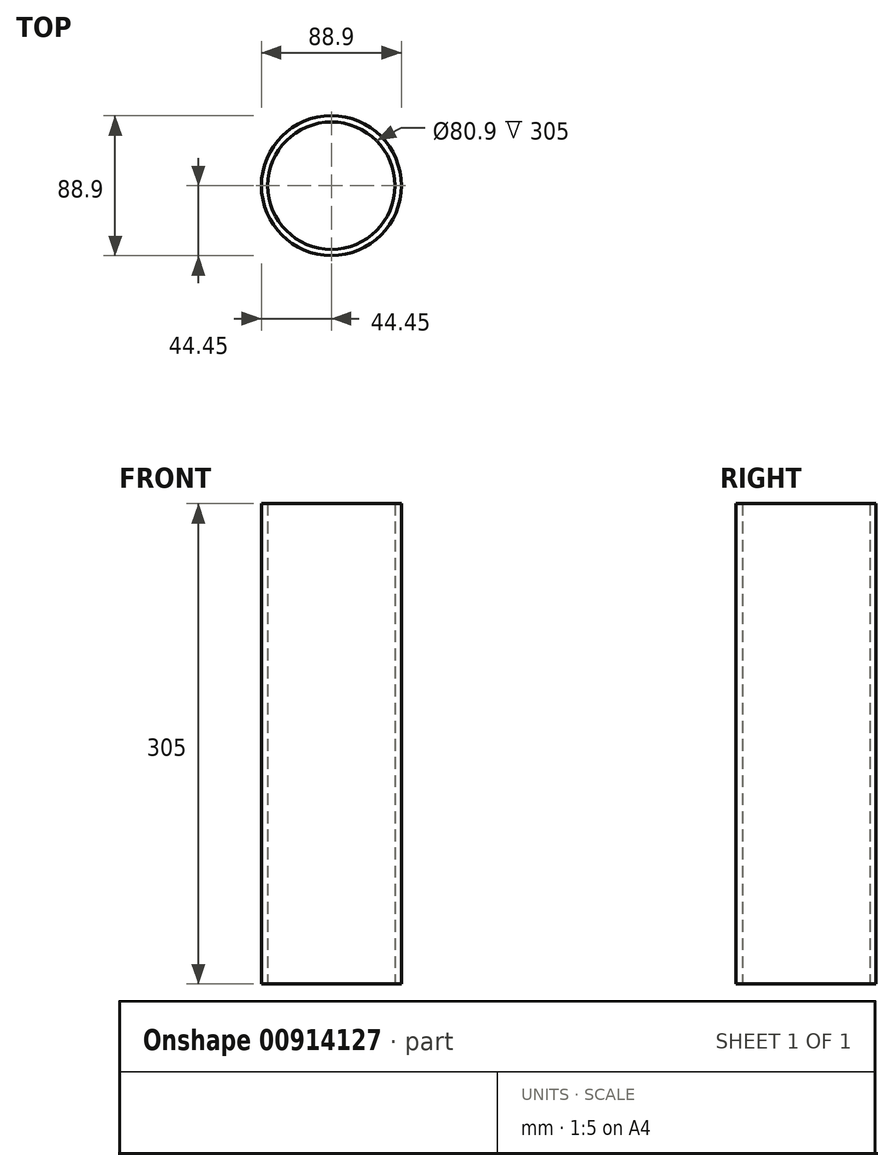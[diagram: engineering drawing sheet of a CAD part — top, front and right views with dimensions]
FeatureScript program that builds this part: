
annotation { "Feature Type Name" : "Feature", "Feature Type Description" : "" }
export const myFeature = defineFeature(function(context is Context, id is Id, definition is map)
    precondition{}
    {
        {
            var Q0;
            Q0=qCreatedBy(makeId("Top.planeOp"),FACE);
            var sketch = newSketch(context, id + "F0", { "sketchPlane" : qUnion([Q0])});
            skCircle(sketch, "E0", {"center": v(0, 0) * mm, "radius": 44.45 * mm});
            skCircle(sketch, "E1.0", {"center": v(0, 0) * mm, "radius": 40.45 * mm});
            skSolve(sketch);
        }
        {
            var Q0;
            Q0=makeQuery(id+"F0.imprint","IMPRINT",FACE,{"disambiguationData":[TD([[makeQuery(id+"F0.imprint","IMPRINT",EDGE,{"derivedFrom":sQuery(id+"F0.wireOp",EDGE,"E0")}),1.0]])]});
            extrude(context, id + "F1", {"entities" : qUnion([Q0]), "depth" : 305 * mm, "offsetDistance" : 25 * mm});
        }
    });
